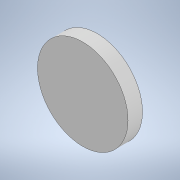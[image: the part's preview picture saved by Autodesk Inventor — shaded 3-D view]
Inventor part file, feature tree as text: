
AUTODESK INVENTOR PART (.ipt)
format: ipt  version: 2020 (Build 240168000, 168)  size: 92,160 bytes
history: native  units: mm
features: extrude x1, sketch x1
ambient origin geometry x8: Origin, YZ Plane, XZ Plane, XY Plane, X Axis, Y Axis, Z Axis, Center Point
bodies: Solid1 (feature_tree)
feature tree (2):
  extrude  "Extrusion1"  Depth=40.0mm TaperAngle=0.0deg
  sketch  "Sketch1"  dims[d1=250.0mm d2=40.0mm d3=0.0mm]
